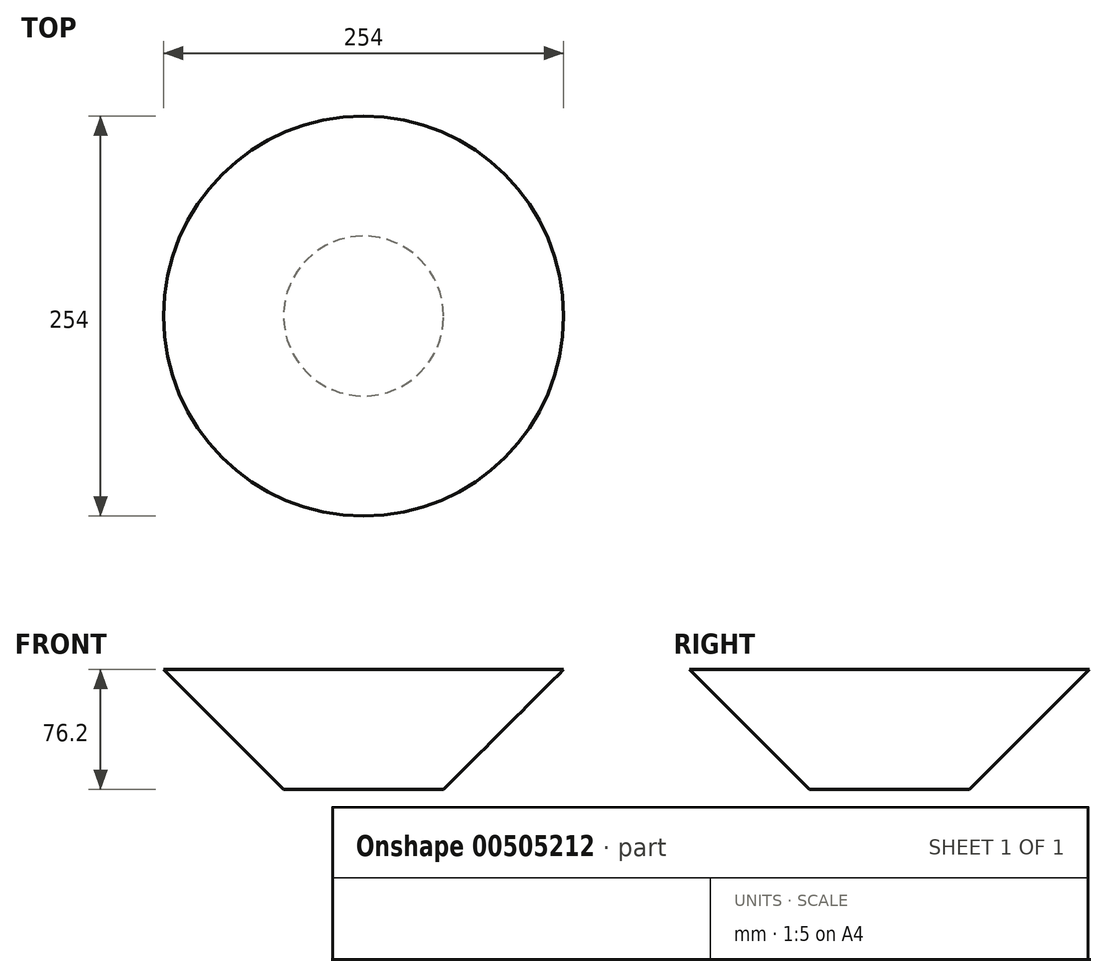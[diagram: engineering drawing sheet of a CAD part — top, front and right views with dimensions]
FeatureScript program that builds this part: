
annotation { "Feature Type Name" : "Feature", "Feature Type Description" : "" }
export const myFeature = defineFeature(function(context is Context, id is Id, definition is map)
    precondition{}
    {
        {
            var Q0;
            Q0=qCreatedBy(makeId("Top.planeOp"),FACE);
            var sketch = newSketch(context, id + "F0", { "sketchPlane" : qUnion([Q0])});
            skPoint(sketch, "E0.middle", {"position": v(0, 0) * mm});
            skCircle(sketch, "E1", {"center": v(0, 0) * mm, "radius": 50.8 * mm});
            skSolve(sketch);
        }
        {
            var Q0;
            Q0=qCreatedBy(makeId("Top.planeOp"),FACE);
            cPlane(context, id + "F1", {"entities" : qUnion([Q0]), "cplaneType" : CPlaneType.OFFSET, "offset" : 76.2 * mm, "width" : 152.4 * mm, "height" : 152.4 * mm});
        }
        {
            var Q0;
            Q0=qCreatedBy(id+"F1.planeOp",FACE);
            var sketch = newSketch(context, id + "F2", { "sketchPlane" : qUnion([Q0])});
            skCircle(sketch, "E2", {"center": v(0, 0) * mm, "radius": 127 * mm});
            skSolve(sketch);
        }
        {
            var Q0;
            Q0=makeQuery(id+"F2.imprint","IMPRINT",FACE,{"disambiguationData":[TD([[makeQuery(id+"F2.imprint","IMPRINT",EDGE,{"derivedFrom":sQuery(id+"F2.wireOp",EDGE,"E2")}),1.0]])]});
            var Q1;
            Q1=makeQuery(id+"F0.imprint","IMPRINT",FACE,{"disambiguationData":[TD([[makeQuery(id+"F0.imprint","IMPRINT",EDGE,{"derivedFrom":sQuery(id+"F0.wireOp",EDGE,"E1")}),1.0]])]});
            loft(context, id + "F3", {"sheetProfilesArray" : [{ "sheetProfileEntities" : qUnion([Q0]) }, { "sheetProfileEntities" : qUnion([Q1]) }]});
        }
    });
